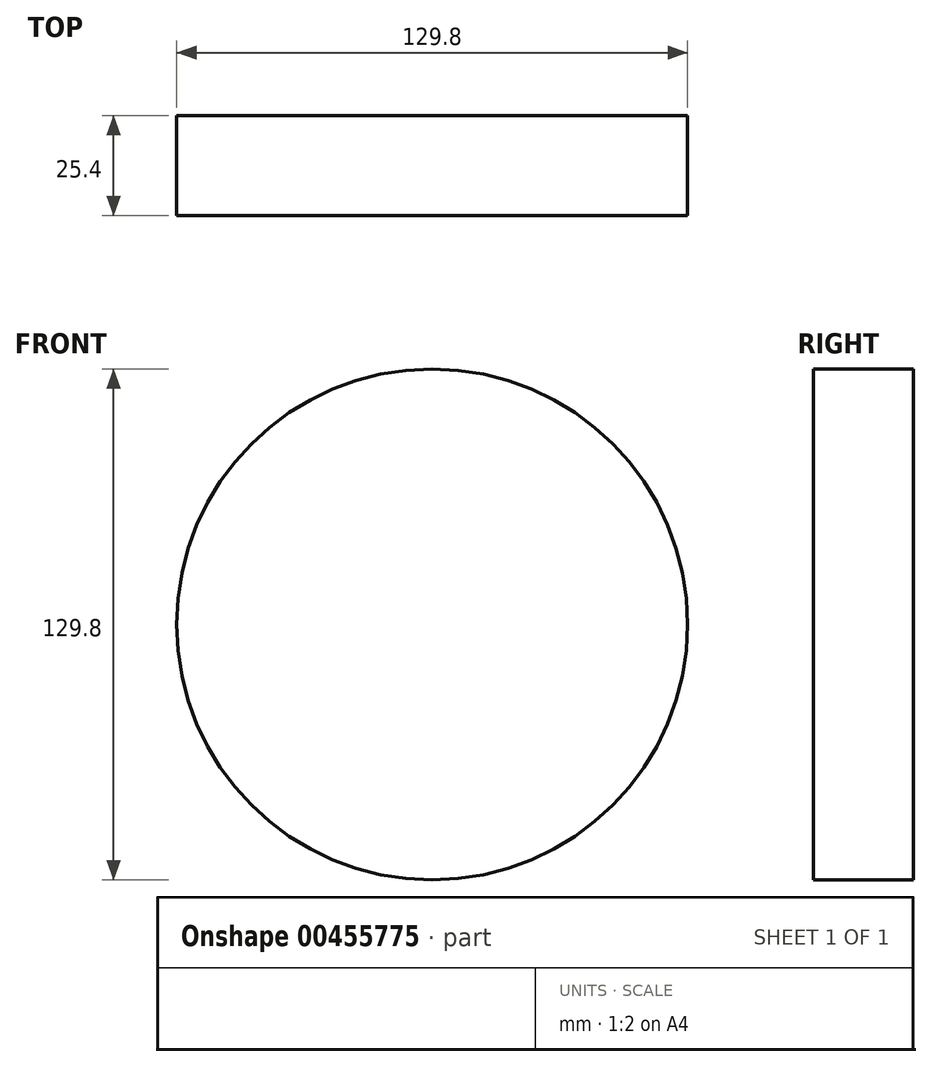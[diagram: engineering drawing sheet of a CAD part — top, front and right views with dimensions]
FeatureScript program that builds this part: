
annotation { "Feature Type Name" : "Feature", "Feature Type Description" : "" }
export const myFeature = defineFeature(function(context is Context, id is Id, definition is map)
    precondition{}
    {
        {
            var Q0;
            Q0=qCreatedBy(makeId("Front.planeOp"),FACE);
            var sketch = newSketch(context, id + "F0", { "sketchPlane" : qUnion([Q0])});
            skCircle(sketch, "E0", {"center": v(7.05, 6.46) * mm, "radius": 44 * mm});
            skPoint(sketch, "E0.first.point", {"position": v(-9.27, 47.32) * mm});
            skPoint(sketch, "E0.second.point", {"position": v(16.1, -36.59) * mm});
            skPoint(sketch, "E0.third.point", {"position": v(-32.44, -12.93) * mm});
            skCircle(sketch, "E1", {"center": v(5.1, 13.38) * mm, "radius": 31.04 * mm});
            skPoint(sketch, "E1.first.point", {"position": v(2.68, -17.56) * mm});
            skPoint(sketch, "E1.second.point", {"position": v(6.34, 44.4) * mm});
            skPoint(sketch, "E1.third.point", {"position": v(26.59, -9.03) * mm});
            skCircle(sketch, "E2", {"center": v(0.58, 18.26) * mm, "radius": 18.12 * mm});
            skPoint(sketch, "E2.first.point", {"position": v(10.98, 3.42) * mm});
            skPoint(sketch, "E2.second.point", {"position": v(-5.37, 35.37) * mm});
            skPoint(sketch, "E2.third.point", {"position": v(-13.17, 6.46) * mm});
            skCircle(sketch, "E3", {"center": v(2.02, 20.34) * mm, "radius": 10.59 * mm});
            skPoint(sketch, "E3.first.point", {"position": v(2.2, 9.76) * mm});
            skPoint(sketch, "E3.second.point", {"position": v(0, 30.74) * mm});
            skPoint(sketch, "E3.third.point", {"position": v(-8.54, 19.51) * mm});
            skCircle(sketch, "E4", {"center": v(4.8, 10.18) * mm, "radius": 37.34 * mm});
            skPoint(sketch, "E4.first.point", {"position": v(19.51, -24.15) * mm});
            skPoint(sketch, "E4.second.point", {"position": v(-11.22, 43.9) * mm});
            skPoint(sketch, "E4.third.point", {"position": v(19.76, 44.4) * mm});
            skCircle(sketch, "E5", {"center": v(4.89, 5.85) * mm, "radius": 52.44 * mm});
            skPoint(sketch, "E5.first.point", {"position": v(44.88, 39.76) * mm});
            skPoint(sketch, "E5.second.point", {"position": v(-32.44, -30.98) * mm});
            skPoint(sketch, "E5.third.point", {"position": v(-40.74, -20) * mm});
            skCircle(sketch, "E6", {"center": v(9.83, 2.1) * mm, "radius": 64.9 * mm});
            skPoint(sketch, "E6.first.point", {"position": v(-29.52, -49.52) * mm});
            skPoint(sketch, "E6.second.point", {"position": v(40.98, 59.03) * mm});
            skPoint(sketch, "E6.third.point", {"position": v(14.4, 66.84) * mm});
            skSolve(sketch);
        }
        {
            var Q0;
            Q0 = qSketchRegion(id + "F0", true);
            var Q1;
            Q1=makeQuery(id+"F0.imprint","IMPRINT",FACE,{"disambiguationData":[TD([[makeQuery(id+"F0.imprint","IMPRINT",EDGE,{"derivedFrom":sQuery(id+"F0.wireOp",EDGE,"E0")}),-1.0]])]});
            var Q2;
            Q2=makeQuery(id+"F0.imprint","IMPRINT",FACE,{"disambiguationData":[TD([[makeQuery(id+"F0.imprint","IMPRINT",EDGE,{"derivedFrom":sQuery(id+"F0.wireOp",EDGE,"E1")}),-1.0]])]});
            var Q3;
            Q3=makeQuery(id+"F0.imprint","IMPRINT",FACE,{"disambiguationData":[TD([[makeQuery(id+"F0.imprint","IMPRINT",EDGE,{"derivedFrom":sQuery(id+"F0.wireOp",EDGE,"E0")}),1.0]])]});
            var Q4;
            Q4=makeQuery(id+"F0.imprint","IMPRINT",FACE,{"disambiguationData":[TD([[makeQuery(id+"F0.imprint","IMPRINT",EDGE,{"derivedFrom":sQuery(id+"F0.wireOp",EDGE,"E1")}),1.0]])]});
            var Q5;
            Q5=makeQuery(id+"F0.imprint","IMPRINT",FACE,{"disambiguationData":[TD([[makeQuery(id+"F0.imprint","IMPRINT",EDGE,{"derivedFrom":sQuery(id+"F0.wireOp",EDGE,"E3")}),1.0]])]});
            var Q6;
            Q6=makeQuery(id+"F0.imprint","IMPRINT",FACE,{"disambiguationData":[TD([[makeQuery(id+"F0.imprint","IMPRINT",EDGE,{"derivedFrom":sQuery(id+"F0.wireOp",EDGE,"E2")}),1.0]])]});
            extrude(context, id + "F1", {"entities" : qUnion([Q0, Q1, Q2, Q3, Q4, Q5, Q6]), "depth" : 25.4 * mm});
        }
    });
